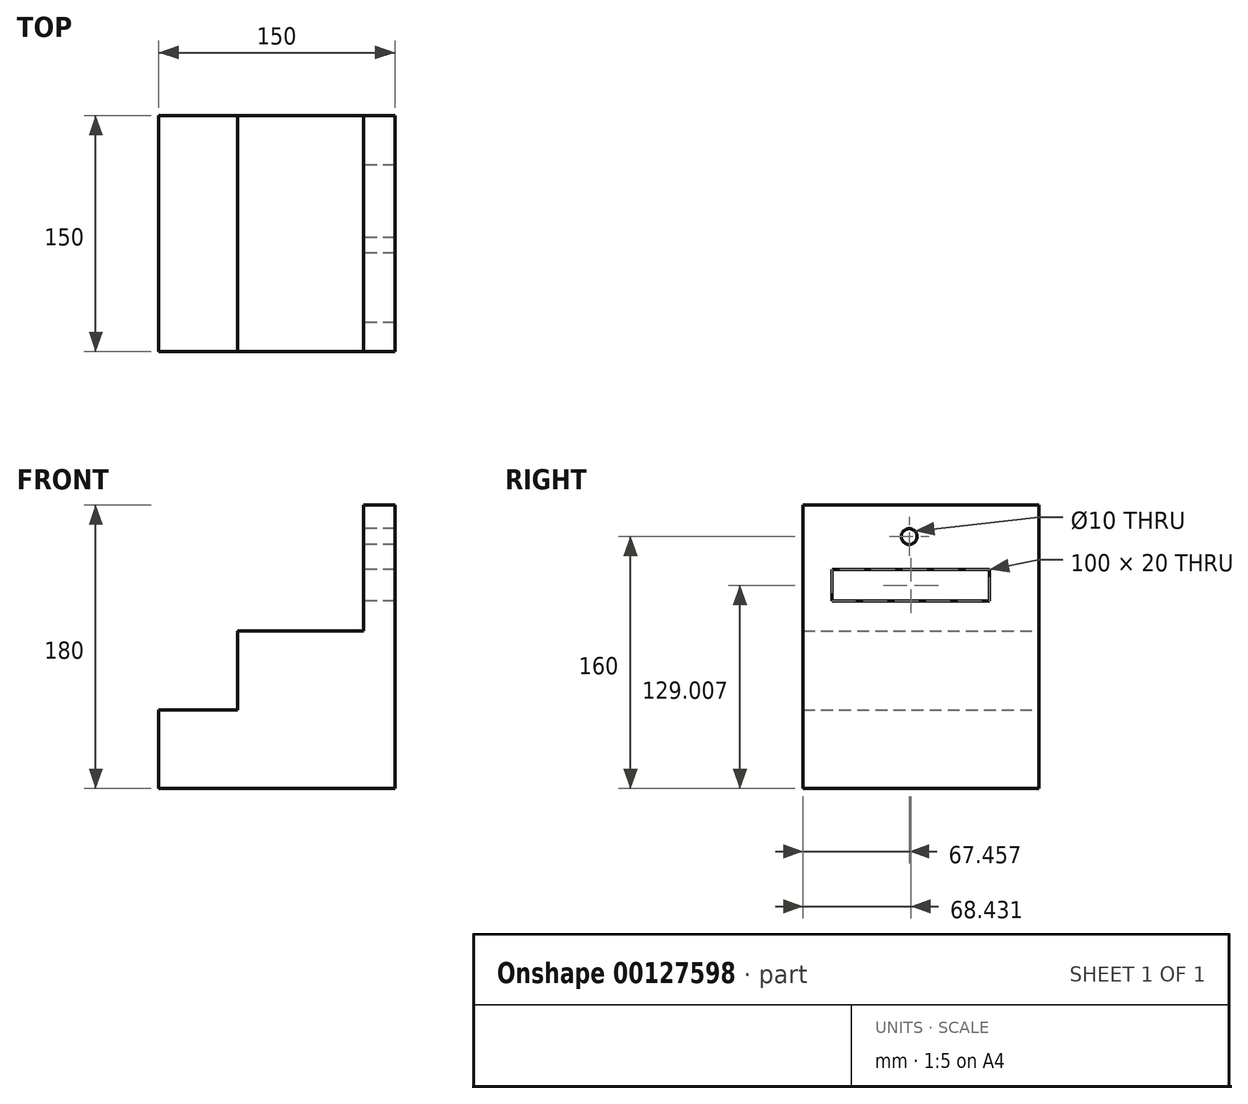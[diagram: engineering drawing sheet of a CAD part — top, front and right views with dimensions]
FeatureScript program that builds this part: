
annotation { "Feature Type Name" : "Feature", "Feature Type Description" : "" }
export const myFeature = defineFeature(function(context is Context, id is Id, definition is map)
    precondition{}
    {
        {
            var Q0;
            Q0=qCreatedBy(makeId("Front.planeOp"),FACE);
            var sketch = newSketch(context, id + "F0", { "sketchPlane" : qUnion([Q0])});
            skLineSegment(sketch, "E0.bottom", {"start": v(55.1, 90) * mm, "end": v(75, 90) * mm});
            skLineSegment(sketch, "E0.top", {"start": v(-75, -90) * mm, "end": v(75, -90) * mm});
            skLineSegment(sketch, "E0.left", {"start": v(-75, -40) * mm, "end": v(-75, -90) * mm});
            skLineSegment(sketch, "E0.right", {"start": v(75, 90) * mm, "end": v(75, -90) * mm});
            skPoint(sketch, "E0.middle", {"position": v(0, 0) * mm});
            skPoint(sketch, "E1.end.orphan", {"position": v(0, -40) * mm});
            skPoint(sketch, "E2.start.orphan", {"position": v(53.12, 0) * mm});
            skLineSegment(sketch, "E3", {"start": v(75, 90) * mm, "end": v(55.1, 90) * mm});
            skLineSegment(sketch, "E4", {"start": v(55.1, 90) * mm, "end": v(55.1, 10) * mm});
            skLineSegment(sketch, "E5", {"start": v(55.1, 10) * mm, "end": v(-24.9, 10) * mm});
            skLineSegment(sketch, "E6", {"start": v(-24.9, 10) * mm, "end": v(-24.9, -40) * mm});
            skLineSegment(sketch, "E7", {"start": v(-24.9, -40) * mm, "end": v(-75, -40) * mm});
            skLineSegment(sketch, "E8", {"start": v(-75, -40) * mm, "end": v(-75.33, -90) * mm});
            skPoint(sketch, "E9.orphan", {"position": v(-75, 90) * mm});
            skSolve(sketch);
        }
        {
            var Q0;
            Q0 = qSketchRegion(id + "F0", true);
            extrude(context, id + "F1", {"entities" : qUnion([Q0]), "depth" : 150 * mm});
        }
        {
            var Q0;
            Q0=makeQuery(id+"F1.opExtrude","SWEPT_FACE",FACE,{"disambiguationData":[OSD([sQuery(id+"F0.wireOp",EDGE,"E4")])]});
            var sketch = newSketch(context, id + "F2", { "sketchPlane" : qUnion([Q0])});
            skCircle(sketch, "E10", {"center": v(82.54, 70) * mm, "radius": 5 * mm});
            skSolve(sketch);
        }
        {
            var Q0;
            Q0=makeQuery(id+"F2.imprint","IMPRINT",FACE,{"disambiguationData":[TD([[makeQuery(id+"F2.imprint","IMPRINT",EDGE,{"derivedFrom":sQuery(id+"F2.wireOp",EDGE,"E10")}),1.0]])]});
            extrude(context, id + "F3", {"entities" : qUnion([Q0]), "operationType" : NewBodyOperationType.REMOVE, "endBound" : BoundingType.THROUGH_ALL, "oppositeDirection" : true, "depth" : 25.4 * mm});
        }
        {
            var Q0;
            Q0=makeQuery(id+"F1.opExtrude","SWEPT_FACE",FACE,{"disambiguationData":[OSD([sQuery(id+"F0.wireOp",EDGE,"E4")])]});
            var sketch = newSketch(context, id + "F4", { "sketchPlane" : qUnion([Q0])});
            skLineSegment(sketch, "E11.bottom", {"start": v(31.57, 49) * mm, "end": v(131.57, 49) * mm});
            skLineSegment(sketch, "E11.top", {"start": v(31.57, 29) * mm, "end": v(131.57, 29) * mm});
            skLineSegment(sketch, "E11.left", {"start": v(31.57, 49) * mm, "end": v(31.57, 29) * mm});
            skLineSegment(sketch, "E11.right", {"start": v(131.57, 49) * mm, "end": v(131.57, 29) * mm});
            skSolve(sketch);
        }
        {
            var Q0;
            Q0=makeQuery(id+"F4.imprint","IMPRINT",FACE,{"disambiguationData":[TD([[makeQuery(id+"F4.imprint","IMPRINT",EDGE,{"derivedFrom":sQuery(id+"F4.wireOp",EDGE,"E11.bottom")}),-1.0]])]});
            extrude(context, id + "F5", {"entities" : qUnion([Q0]), "operationType" : NewBodyOperationType.REMOVE, "endBound" : BoundingType.THROUGH_ALL, "oppositeDirection" : true, "depth" : 25.4 * mm});
        }
    });
